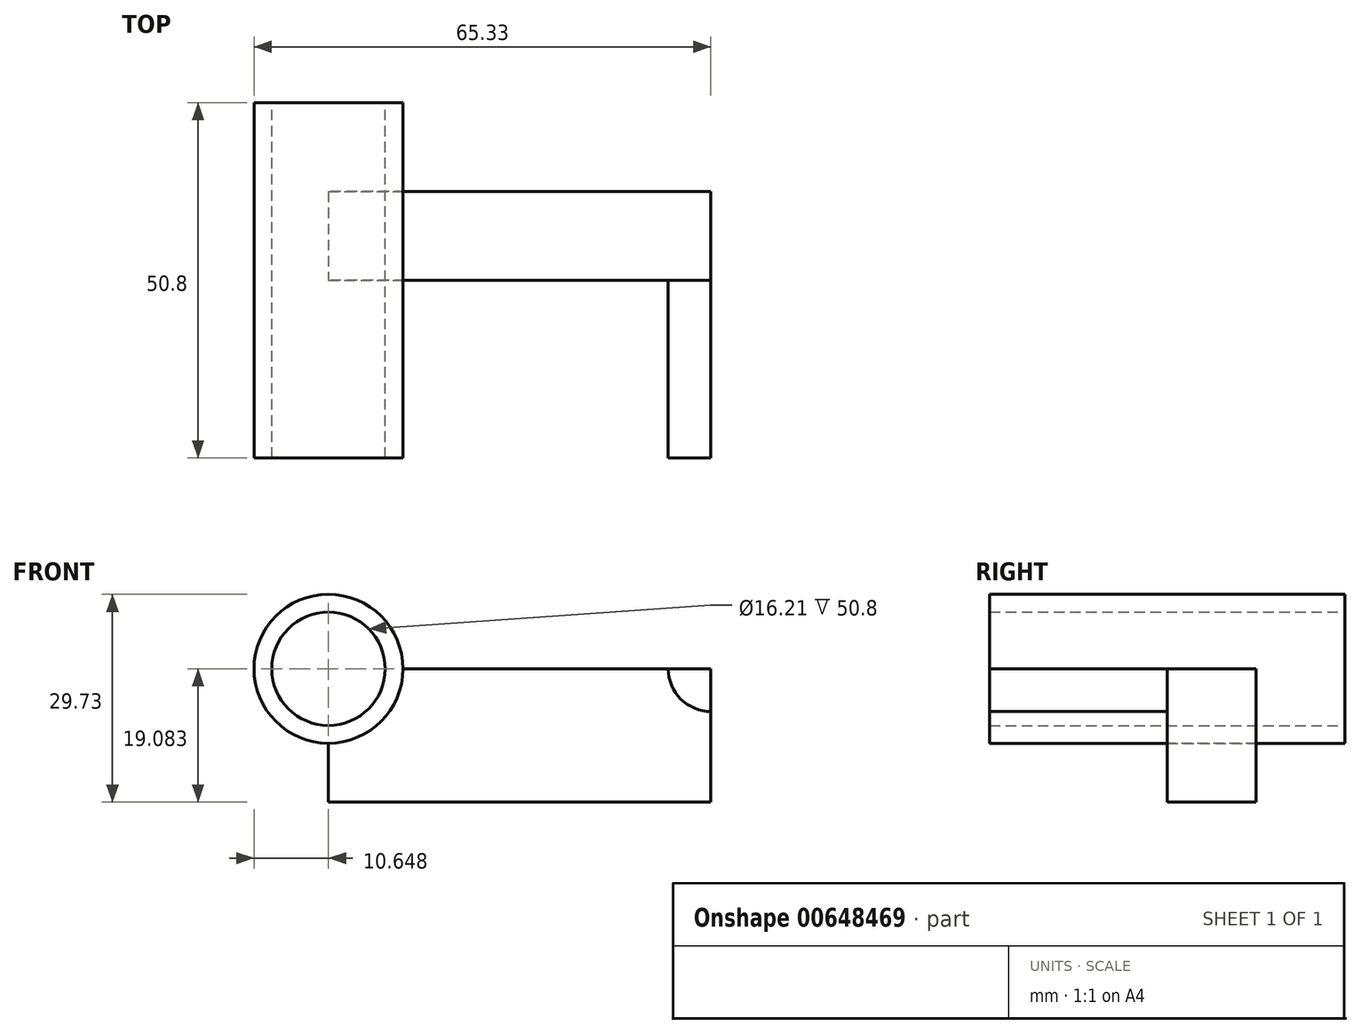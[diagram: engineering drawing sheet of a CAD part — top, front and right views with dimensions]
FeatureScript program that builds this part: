
annotation { "Feature Type Name" : "Feature", "Feature Type Description" : "" }
export const myFeature = defineFeature(function(context is Context, id is Id, definition is map)
    precondition{}
    {
        {
            var Q0;
            Q0=qCreatedBy(makeId("Front.planeOp"),FACE);
            var sketch = newSketch(context, id + "F0", { "sketchPlane" : qUnion([Q0])});
            skLineSegment(sketch, "E0.bottom", {"start": v(27.34, 9.54) * mm, "end": v(-27.34, 9.54) * mm});
            skLineSegment(sketch, "E0.top", {"start": v(27.34, -9.54) * mm, "end": v(-27.34, -9.54) * mm});
            skLineSegment(sketch, "E0.left", {"start": v(27.34, 9.54) * mm, "end": v(27.34, -9.54) * mm});
            skLineSegment(sketch, "E0.right", {"start": v(-27.34, 9.54) * mm, "end": v(-27.34, -9.54) * mm});
            skPoint(sketch, "E0.middle", {"position": v(0, 0) * mm});
            skCircle(sketch, "E1", {"center": v(-27.34, 9.54) * mm, "radius": 10.65 * mm});
            skCircle(sketch, "E2", {"center": v(27.34, 9.54) * mm, "radius": 6.1 * mm});
            skSolve(sketch);
        }
        {
            var Q0;
            Q0=qCreatedBy(makeId("Top.planeOp"),FACE);
            var sketch = newSketch(context, id + "F1", { "sketchPlane" : qUnion([Q0])});
            skLineSegment(sketch, "E3", {"start": v(-62.3, -54.58) * mm, "end": v(59.38, -67.6) * mm});
            skLineSegment(sketch, "E4", {"start": v(59.38, -67.6) * mm, "end": v(18.23, -36.74) * mm});
            skSolve(sketch);
        }
        {
            var Q0;
            Q0=sQuery(id+"F0.wireOp",EDGE,"E0.top");
            cPlane(context, id + "F2", {"entities" : qUnion([Q0]), "cplaneType" : CPlaneType.LINE_ANGLE, "offset" : 25.4 * mm, "angle" : 33 * degree, "width" : 152.4 * mm, "height" : 152.4 * mm});
        }
        {
            var Q0;
            {var subQ0=sQuery(id+"F0.wireOp",EDGE,"E0.right");var subQ1=sQuery(id+"F0.wireOp",EDGE,"E0.bottom");var subQ2=makeQuery(id+"F0.imprint","INTERSECT",VERTEX,{"derivedFrom":[subQ1,subQ0]});Q0=makeQuery(id+"F0.imprint","IMPRINT",FACE,{"disambiguationData":[TD([[makeQuery(id+"F0.imprint","IMPRINT",EDGE,{"disambiguationData":[TD([[subQ2,1.0]])],"derivedFrom":subQ1}),-1.0]])]});}
            var Q1;
            {var subQ0=sQuery(id+"F0.wireOp",EDGE,"E0.right");var subQ1=sQuery(id+"F0.wireOp",EDGE,"E0.bottom");var subQ2=makeQuery(id+"F0.imprint","INTERSECT",VERTEX,{"derivedFrom":[subQ1,subQ0]});Q1=makeQuery(id+"F0.imprint","IMPRINT",FACE,{"disambiguationData":[TD([[makeQuery(id+"F0.imprint","IMPRINT",EDGE,{"disambiguationData":[TD([[subQ2,1.0]])],"derivedFrom":subQ1}),1.0]])]});}
            extrude(context, id + "F3", {"entities" : qUnion([Q0, Q1]), "endBound" : BoundingType.SYMMETRIC, "depth" : 50.8 * mm, "offsetDistance" : 25.4 * mm});
        }
        {
            var Q0;
            {var subQ0=sQuery(id+"F0.wireOp",EDGE,"E0.left");var subQ1=sQuery(id+"F0.wireOp",EDGE,"E0.bottom");var subQ2=makeQuery(id+"F0.imprint","INTERSECT",VERTEX,{"derivedFrom":[subQ1,subQ0]});Q0=makeQuery(id+"F0.imprint","IMPRINT",FACE,{"disambiguationData":[TD([[makeQuery(id+"F0.imprint","IMPRINT",EDGE,{"disambiguationData":[TD([[subQ2,-1.0]])],"derivedFrom":subQ1}),1.0]])]});}
            extrude(context, id + "F4", {"entities" : qUnion([Q0]), "depth" : 25.4 * mm, "offsetDistance" : 25.4 * mm});
        }
        {
            var Q0;
            {var subQ1=sQuery(id+"F0.wireOp",EDGE,"E0.top");Q0=makeQuery(id+"F0.imprint","IMPRINT",FACE,{"disambiguationData":[TD([[makeQuery(id+"F0.imprint","IMPRINT",EDGE,{"derivedFrom":subQ1}),-1.0]])]});}
            var Q1;
            {var subQ0=sQuery(id+"F0.wireOp",EDGE,"E0.left");var subQ1=sQuery(id+"F0.wireOp",EDGE,"E0.bottom");var subQ2=makeQuery(id+"F0.imprint","INTERSECT",VERTEX,{"derivedFrom":[subQ1,subQ0]});Q1=makeQuery(id+"F0.imprint","IMPRINT",FACE,{"disambiguationData":[TD([[makeQuery(id+"F0.imprint","IMPRINT",EDGE,{"disambiguationData":[TD([[subQ2,-1.0]])],"derivedFrom":subQ1}),1.0]])]});}
            extrude(context, id + "F5", {"entities" : qUnion([Q0, Q1]), "depth" : -12.7 * mm, "offsetDistance" : 25.4 * mm});
        }
        {
            var Q0;
            Q0=makeQuery(id+"F3.opExtrude","CAP_FACE",FACE,{"disambiguationData":[OSD([sQuery(id+"F0.wireOp",EDGE,"E1")])],"isStart":false});
            var Q1;
            Q1=makeQuery(id+"F3.opExtrude","CAP_FACE",FACE,{"disambiguationData":[OSD([sQuery(id+"F0.wireOp",EDGE,"E1")])],"isStart":true});
            shell(context, id + "F6", {"entities" : qUnion([Q0, Q1]), "thickness" : 2.54 * mm});
        }
    });
